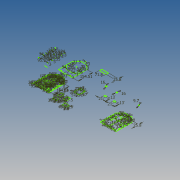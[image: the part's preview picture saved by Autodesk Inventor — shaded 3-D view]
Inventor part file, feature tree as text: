
AUTODESK INVENTOR PART (.ipt)
format: ipt  version: 2014 (Build 180170000, 170)  size: 356,864 bytes
history: native  units: mm
features: sketch x4
ambient origin geometry x8: Origin, YZ Plane, XZ Plane, XY Plane, X Axis, Y Axis, Z Axis, Center Point
feature tree (4):
  sketch  "Sketch1"  dims[d7=71.8mm]
  sketch  "Sketch2"  dims[d8=25.8mm]
  sketch  "Sketch3"  dims[d9=16.0mm]
  sketch  "Sketch4"  dims[d10=16.0mm d11=9.7mm d12=21.0mm d13=13.0mm d14=21.0mm d15=13.0mm d18=154.51mm d21=154.51mm d25=10.0mm d26=10.0mm d27=2.0mm d28=17.0mm d29=1.0mm d30=10.0mm d31=2.0mm d32=17.0mm d33=10.0mm d34=2.0mm d37=1.0mm d39=17.0mm d40=10.0mm d41=2.0mm d42=10.0mm d43=10.0mm d44=2.0mm d45=10.0mm d46=2.0mm d47=10.0mm d50=17.0mm d51=17.0mm d52=15.0mm d53=2.0mm d54=1.0mm d56=15.0mm d57=18.0mm d58=15.0mm d59=17.0mm d63=2.0mm d64=15.0mm d65=1.0mm d72=15.0mm d73=18.0mm d74=15.0mm d75=17.0mm d76=15.0mm d77=18.0mm d78=20.673333mm d80=20.836667mm d81=154.51mm d87=15.0mm d88=20.836667mm d92=18.0mm d93=219.764931mm d95=174.51mm d97=3.0mm d98=3.0mm d99=3.0mm d100=3.0mm d101=3.0mm d102=-5.117mm d103=10.0mm d104=15.117mm d105=10.0mm d106=5.554212mm d107=5.0mm d108=5.0mm d109=5.554212mm d110=5.554212mm d111=5.0mm d112=5.0mm d115=19.420788mm d116=60.018569mm d117=3.0mm d118=3.0mm d119=3.0mm d120=5.117mm d121=0.0mm d122=15.117007mm d123=3.0mm d124=5.0mm d125=5.0mm d126=5.0mm d127=5.000007mm d128=5.0mm d131=24.975mm d132=55.031431mm d133=60.0mm d134=25.0mm d135=30.0mm d136=3.0mm d137=12.5mm d138=57.0mm d139=67.0mm d140=3.0mm d141=3.0mm d142=3.0mm d143=51.0mm d144=51.0mm d145=51.0mm d146=51.0mm d147=3.0mm d151=2.0mm d152=12.0mm d153=12.0mm d154=11.0mm d155=11.0mm d156=3.0mm d157=3.0mm d158=3.0mm d159=2.0mm d160=12.0mm d161=12.0mm d162=14.0mm d163=11.0mm d164=154.51mm d168=3.0mm d169=8.0mm d170=8.0mm d171=3.0mm d172=8.0mm d173=8.0mm d176=10.0mm d177=2.0mm d180=10.0mm d181=2.0mm d183=10.0mm d184=2.0mm d187=10.0mm d188=2.0mm d189=10.0mm d190=10.0mm d191=2.0mm d192=10.0mm d193=2.0mm d194=10.0mm d197=15.0mm d198=2.0mm d200=15.0mm d201=18.0mm d202=15.0mm d203=17.0mm d204=2.0mm d205=15.0mm d207=15.0mm d208=18.0mm d209=15.0mm d210=17.0mm d211=15.0mm d212=18.0mm d216=15.0mm d219=18.0mm d220=219.764931mm d221=174.51mm d264=3.0mm d267=3.0mm d270=71.8mm d271=25.8mm d273=35.0mm d274=16.0mm d275=50.0mm d276=25.0mm d277=13.0mm d278=21.0mm d280=40.0mm d281=9.7mm d282=20.0mm d283=3.0mm d284=3.0mm d285=3.0mm d286=3.0mm d287=3.0mm d288=3.0mm d289=35.0mm d290=3.0mm d291=30.0mm d292=34.23504mm d293=34.23504mm d294=35.0mm d295=30.0mm d296=31.5mm d297=31.5mm d298=3.0mm d299=3.0mm d300=3.0mm d302=3.0mm d304=35.0mm d305=3.0mm d306=30.0mm d307=34.23504mm d308=34.23504mm d309=35.0mm d310=30.0mm d311=31.5mm d312=31.5mm d313=95.933639mm d314=95.933639mm d315=95.933639mm d316=95.933639mm d317=95.933639mm d318=95.933639mm d321=3.0mm d322=3.0mm d332=95.933639mm d335=95.933639mm d337=95.933639mm d339=50.0mm d341=25.0mm d342=30.0mm d343=60.0mm d344=5.0mm d345=110.0mm d346=20.0mm d347=55.0mm d349=10.0mm d350=5.0mm d351=28.5mm d352=44.6mm d353=3.0mm d354=3.0mm d355=2.2mm d356=23.7mm d357=2.2mm d358=39.8mm d359=32.7mm d360=45.5mm d361=2.6mm d362=2.6mm d363=27.4mm d364=40.4mm d365=44.6mm d366=28.5mm d367=3.0mm d368=3.0mm d369=2.2mm d370=2.2mm d371=23.7mm d372=39.8mm d373=45.5mm d374=32.7mm d375=3.0mm d376=3.0mm d377=2.6mm d378=2.6mm d379=27.4mm d380=40.4mm d385=27.4mm d386=40.4mm d391=3.0mm d392=3.0mm d394=23.7mm d396=39.8mm d399=30.0mm d400=30.0mm d401=5.0mm]
